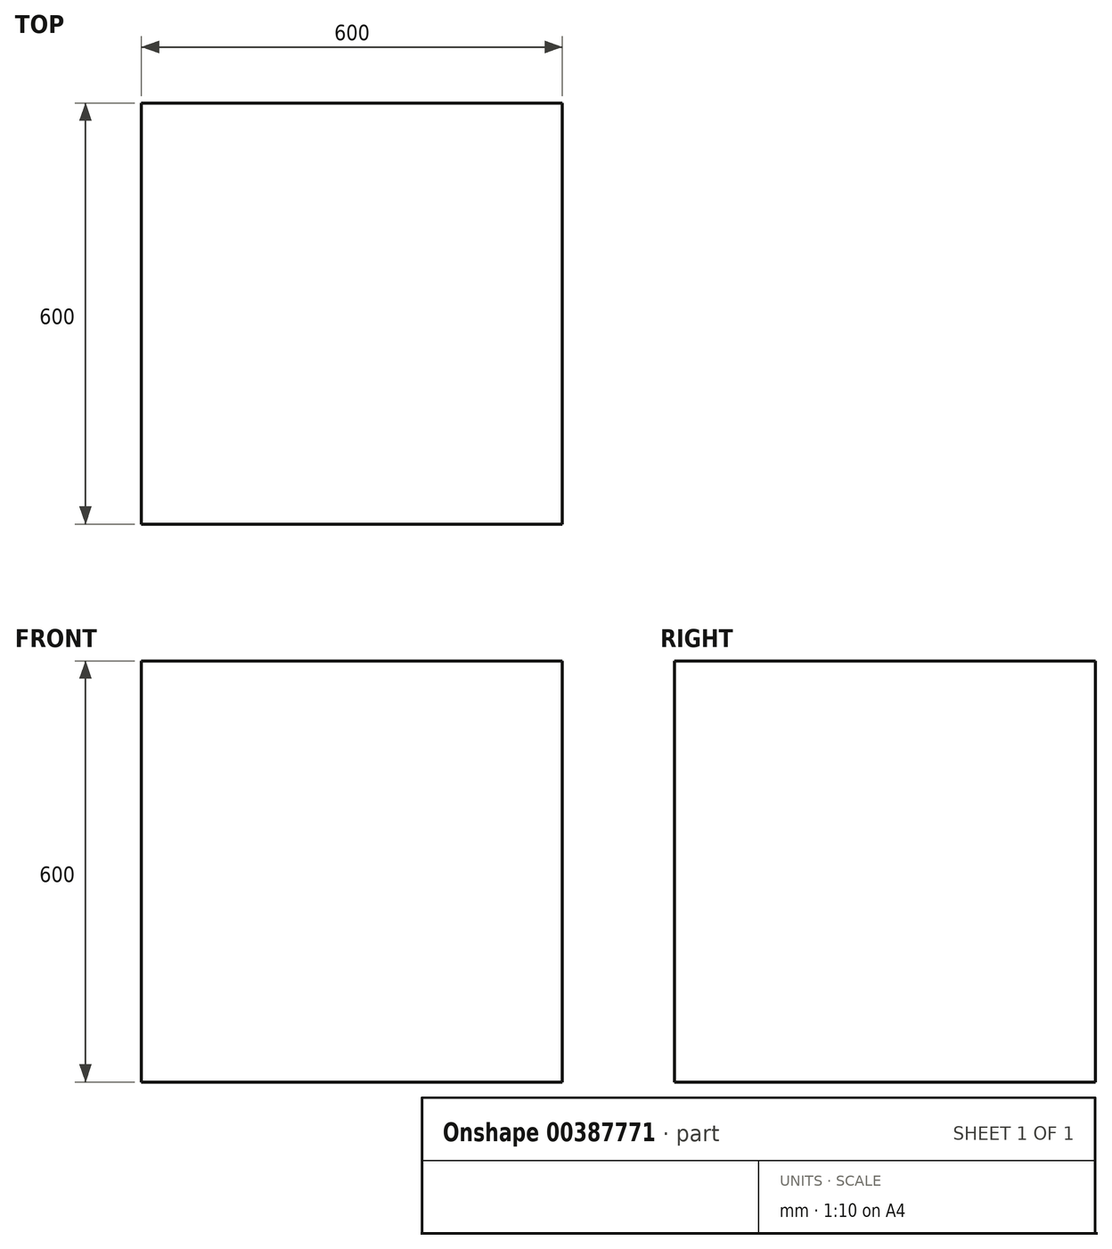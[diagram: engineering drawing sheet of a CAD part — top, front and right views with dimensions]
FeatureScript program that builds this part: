
annotation { "Feature Type Name" : "Feature", "Feature Type Description" : "" }
export const myFeature = defineFeature(function(context is Context, id is Id, definition is map)
    precondition{}
    {
        {
            var Q0;
            Q0=qCreatedBy(makeId("Front.planeOp"),FACE);
            var sketch = newSketch(context, id + "F0", { "sketchPlane" : qUnion([Q0])});
            skLineSegment(sketch, "E0.bottom", {"start": v(300, 300) * mm, "end": v(-300, 300) * mm});
            skLineSegment(sketch, "E0.top", {"start": v(300, -300) * mm, "end": v(-300, -300) * mm});
            skLineSegment(sketch, "E0.left", {"start": v(300, 300) * mm, "end": v(300, -300) * mm});
            skLineSegment(sketch, "E0.right", {"start": v(-300, 300) * mm, "end": v(-300, -300) * mm});
            skPoint(sketch, "E0.middle", {"position": v(0, 0) * mm});
            skSolve(sketch);
        }
        {
            var Q0;
            Q0=makeQuery(id+"F0.imprint","IMPRINT",FACE,{"disambiguationData":[TD([[makeQuery(id+"F0.imprint","IMPRINT",EDGE,{"derivedFrom":sQuery(id+"F0.wireOp",EDGE,"E0.bottom")}),1.0]])]});
            extrude(context, id + "F1", {"entities" : qUnion([Q0]), "depth" : 600 * mm});
        }
        {
            var Q0;
            Q0=makeQuery(id+"F1.opExtrude","SWEPT_FACE",FACE,{"disambiguationData":[OSD([sQuery(id+"F0.wireOp",EDGE,"E0.left")])]});
            var sketch = newSketch(context, id + "F2", { "sketchPlane" : qUnion([Q0])});
            skLineSegment(sketch, "E1.bottom", {"start": v(-600, 150) * mm, "end": v(-25, 150) * mm});
            skLineSegment(sketch, "E1.top", {"start": v(-600, -275) * mm, "end": v(-25, -275) * mm});
            skLineSegment(sketch, "E1.left", {"start": v(-600, 150) * mm, "end": v(-600, -275) * mm});
            skLineSegment(sketch, "E1.right", {"start": v(-25, 150) * mm, "end": v(-25, -275) * mm});
            skSolve(sketch);
        }
        {
            var Q0;
            Q0 = qSketchRegion(id + "F2", true);
            extrude(context, id + "F3", {"entities" : qUnion([Q0]), "operationType" : NewBodyOperationType.REMOVE, "depth" : 25.4 * mm});
        }
    });
